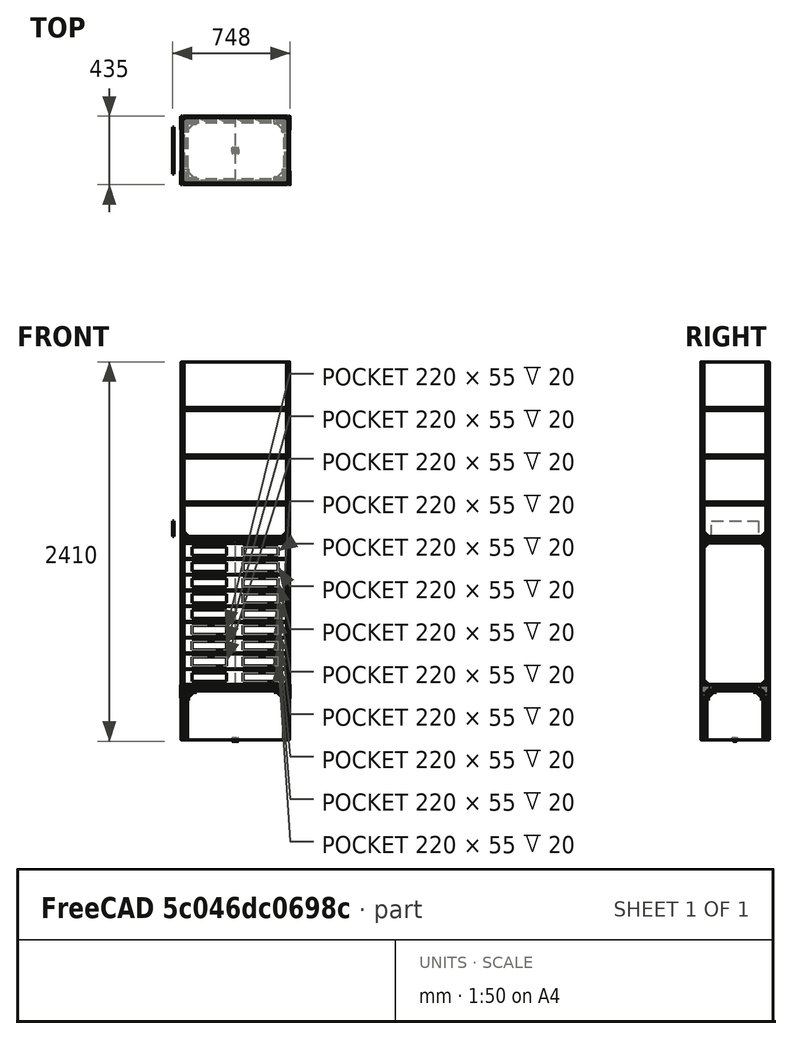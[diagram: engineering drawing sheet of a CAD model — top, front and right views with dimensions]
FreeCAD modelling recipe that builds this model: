
FCSTD DOCUMENT  (FreeCAD 1.0R39109 (Git))
Label: 2020 shelf
License: All rights reserved
objects: Part::FeaturePython×74, PartDesign::SubShapeBinder×16, Sketcher::SketchObject×15, PartDesign::Pad×11, PartDesign::Body×9, App::DocumentObjectGroup×9, PartDesign::Mirrored×7, TechDraw::DrawViewBalloon×7, App::Link×4, TechDraw::DrawProjGroupItem×3, TechDraw::DrawSVGTemplate×2, TechDraw::DrawPage×2, PartDesign::Plane×1, PartDesign::MultiTransform×1, PartDesign::Pocket×1, PartDesign::LinearPattern×1, App::VarSet×1, TechDraw::DrawProjGroup×1
note: 184 computed .brp shape members not serialized (recipe doc carries the construction recipe); baked Part::Feature solids carry a one-line shape summary decoded from their .brp
EXTERNAL_REF file=2020 Parts.FCStd obj=Body
EXTERNAL_REF file=2020 Parts.FCStd obj=Body001
EXTERNAL_REF file=2020 Parts.FCStd obj=Body002
EXTERNAL_REF file=2020 Parts.FCStd obj=Body003

FEATURE [Sketcher::SketchObject] Sketch  label="cabinet projection"
  ArcFitTolerance = 1e-06
  AttachmentSupport = -> [XY_Plane]
  FullyConstrained = true
  MakeInternals = false
  MapMode = 5
  sketch-geometry (5):
    g0: LineSegment StartX=-325 StartY=217.5 StartZ=0 EndX=-325 EndY=-217.5 EndZ=0
    g1: LineSegment StartX=-325 StartY=-217.5 StartZ=0 EndX=325 EndY=-217.5 EndZ=0
    g2: LineSegment StartX=325 StartY=-217.5 StartZ=0 EndX=325 EndY=217.5 EndZ=0
    g3: LineSegment StartX=325 StartY=217.5 StartZ=0 EndX=-325 EndY=217.5 EndZ=0
    g4: GeomPoint [constr] X=0 Y=0 Z=0
  constraints (12):
    c: Coincident(g0,g1)
    c: Coincident(g1,g2)
    c: Coincident(g2,g3)
    c: Coincident(g3,g0)
    c: Vertical(g0)
    c: Vertical(g2)
    c: Horizontal(g1)
    c: Horizontal(g3)
    c: Symmetric(g2,g0,g4)
    c: Coincident(g4,g-1)
    c: DistanceX(g1,g1) = 650
    c: DistanceY(g2,g2) = 435
FEATURE [Sketcher::SketchObject] Sketch001
  ArcFitTolerance = 1e-06
  AttachmentSupport = -> [XY_Plane]
  ExternalGeometry = -> [Sketch]
  FullyConstrained = true
  MakeInternals = false
  MapMode = 5
  sketch-geometry (5):
    g0: LineSegment StartX=335 StartY=207.5 StartZ=0 EndX=-335 EndY=207.5 EndZ=0
    g1: LineSegment StartX=-335 StartY=207.5 StartZ=0 EndX=-335 EndY=-207.5 EndZ=0
    g2: LineSegment StartX=-335 StartY=-207.5 StartZ=0 EndX=335 EndY=-207.5 EndZ=0
    g3: LineSegment StartX=335 StartY=-207.5 StartZ=0 EndX=335 EndY=207.5 EndZ=0
    g4: GeomPoint [constr] X=0 Y=0 Z=0
  constraints (12):
    c: Coincident(g0,g1)
    c: Coincident(g1,g2)
    c: Coincident(g2,g3)
    c: Coincident(g3,g0)
    c: Horizontal(g0)
    c: Horizontal(g2)
    c: Vertical(g1)
    c: Vertical(g3)
    c: Symmetric(g2,g0,g4)
    c: Coincident(g4,g-1)
    c: DistanceY(g-6,g1) = 10
    c: DistanceX(g1,g-6) = 10
FEATURE [PartDesign::Pad] Pad
  Direction = (0,0,1)
  Length = 2400
  Length2 = 10
  Profile = -> Sketch001
  ReferenceAxis = -> Sketch001 [N_Axis]
  Suppressed = false
  Type = 0
FEATURE [PartDesign::SubShapeBinder] Binder
  BindCopyOnChange = 0
  BindMode = 0
  ClaimChildren = false
  Context = -> Body [Binder.]
  Fuse = false
  MakeFace = true
  OffsetFill = false
  OffsetIntersection = false
  OffsetJoinType = 0
  OffsetOpenResult = false
  PartialLoad = false
  Relative = true
  Support = -> [Pad[Edge2,Edge5,Edge8,Edge1]]
  _Version = 2
FEATURE [Sketcher::SketchObject] Sketch002
  ArcFitTolerance = 1e-06
  AttachmentSupport = -> [XY_Plane001]
  FullyConstrained = true
  MakeInternals = false
  MapMode = 5
  sketch-geometry (14):
    g0: LineSegment StartX=0 StartY=3.9 StartZ=0 EndX=2.83934 EndY=3.9 EndZ=0
    g1: LineSegment StartX=2.83934 StartY=3.9 StartZ=0 EndX=5.5 EndY=6.56066 EndZ=0
    g2: LineSegment StartX=5.5 StartY=6.56066 StartZ=0 EndX=5.5 EndY=8 EndZ=0
    g3: LineSegment StartX=5.5 StartY=8 StartZ=0 EndX=3.1 EndY=8 EndZ=0
    g4: LineSegment StartX=3.1 StartY=8 StartZ=0 EndX=3.1 EndY=9.5 EndZ=0
    g5: LineSegment StartX=3.1 StartY=9.5 StartZ=0 EndX=3.6 EndY=9.5 EndZ=0
    g6: LineSegment StartX=3.6 StartY=9.5 StartZ=0 EndX=3.6 EndY=10 EndZ=0
    g7: LineSegment StartX=3.6 StartY=10 StartZ=0 EndX=8.50001 EndY=10 EndZ=0
    g8: LineSegment StartX=0 StartY=0 StartZ=0 EndX=0 EndY=3.9 EndZ=0
    g9: LineSegment [constr] StartX=10 StartY=8.50001 StartZ=0 EndX=10 EndY=0 EndZ=0
    g10: ArcOfCircle [constr] CenterX=8.50001 CenterY=8.50001 CenterZ=0 NormalX=0 NormalY=0 NormalZ=1 AngleXU=0 Radius=1.49999 StartAngle=0 EndAngle=1.5708
    g11: GeomPoint [constr] X=10 Y=10 Z=0
    g12: LineSegment StartX=0 StartY=0 StartZ=0 EndX=9.56066 EndY=9.56066 EndZ=0
    g13: ArcOfCircle CenterX=8.50001 CenterY=8.5 CenterZ=0 NormalX=0 NormalY=0 NormalZ=1 AngleXU=0 Radius=1.5 StartAngle=0.785402 EndAngle=1.57079
  constraints (41):
    c: PointOnObject(g0,g-2)
    c: Horizontal(g0)
    c: Coincident(g0,g1)
    c: Coincident(g1,g2)
    c: Vertical(g2)
    c: Coincident(g2,g3)
    c: Horizontal(g3)
    c: Coincident(g3,g4)
    c: Vertical(g4)
    c: Coincident(g4,g5)
    c: Coincident(g5,g6)
    c: Coincident(g6,g7)
    c: Horizontal(g7)
    c: Coincident(g8,g0)
    c: Vertical(g6)
    c: Horizontal(g5)
    c: Distance(g8,g8) = 3.9
    c: DistanceX(g-1,g11) = 10
    c: DistanceY(g-1,g11) = 10
    c: Distance(g3,g0) = 4.1
    c: Equal(g5,g6)
    c: Distance(g6,g6) = 0.5
    c: DistanceY(g3,g6) = 2
    c: PointOnObject(g9,g-1)
    c: Vertical(g9)
    c: PointOnObject(g11,g7)
    c: PointOnObject(g11,g9)
    c: Tangent(g7,g10) = 1.5708
    c: Tangent(g9,g10) = 1.5708
    c: Coincident(g12,g8)
    c: PointOnObject(g12,g10)
    c: PointOnObject(g10,g12)
    c: Coincident(g13,g7)
    c: Coincident(g13,g12)
    c: Tangent(g13,g10)
    c: Coincident(g8,g-1)
    c: Parallel(g1,g12)
    c: Distance(g0,g12) = 0.75
    c: DistanceX(g-1,g2) = 5.5
    c: DistanceX(g-1,g3) = 3.1
    c: Radius(g13) = 1.5
FEATURE [PartDesign::Pad] Pad001
  Direction = (0,0,1)
  Length = 1
  Length2 = 10
  Profile = -> Sketch002
  ReferenceAxis = -> Sketch002 [N_Axis]
  Suppressed = false
  Type = 0
FEATURE [PartDesign::Plane] DatumPlane
  AttachmentOffset = pos=(0,0,0) rot=(0.862856,0.357407,0.357407;1.71777rad)
  AttachmentSupport = -> [XY_Plane001]
  Length = 82.6027
  MapMode = 5
  Placement = pos=(0,0,0) rot=(0.862856,0.357407,0.357407;1.71777rad)
  ResizeMode = 0
  Width = 61.8921
FEATURE [PartDesign::Mirrored] Mirrored
  MirrorPlane = -> DatumPlane
  Suppressed = false
  TransformMode = 0
FEATURE [PartDesign::Mirrored] Mirrored001
  MirrorPlane = -> YZ_Plane001
  Suppressed = false
  TransformMode = 0
FEATURE [PartDesign::Mirrored] Mirrored002
  MirrorPlane = -> XZ_Plane001
  Suppressed = false
  TransformMode = 0
FEATURE [PartDesign::MultiTransform] MultiTransform
  BaseFeature = -> Pad001
  Refine = true
  Suppressed = false
  TransformMode = 1
  Transformations = -> [Mirrored,Mirrored001,Mirrored002]
FEATURE [PartDesign::SubShapeBinder] Binder001  label="2020 Profile"
  BindCopyOnChange = 0
  BindMode = 0
  ClaimChildren = false
  Context = -> Body001 [Binder001.]
  Fuse = false
  MakeFace = true
  OffsetFill = false
  OffsetIntersection = false
  OffsetJoinType = 0
  OffsetOpenResult = false
  PartialLoad = false
  Relative = true
  Support = -> [MultiTransform[Face34]]
  _Version = 2
FEATURE [PartDesign::Body] Body001  label="2020"
  AllowCompound = true
  Group = -> [Sketch002,Pad001,DatumPlane,MultiTransform,Mirrored,Mirrored001,Mirrored002,Binder001]
  Origin = -> Origin001
  Tip = -> MultiTransform
FEATURE [Part::FeaturePython] Clone  label="2020 Profile001"  # Draft clone (typed FeaturePython)
  AttacherType = Attacher::AttachEngine3D
  Fuse = false
  Objects = -> [Binder001]
  Scale = (1,1,1)
FEATURE [Part::FeaturePython] Clone001  label="Binder001"  # Draft clone (typed FeaturePython)
  AttacherType = Attacher::AttachEngine3D
  Fuse = false
  Objects = -> [Binder]
  Scale = (1,1,1)
FEATURE [Part::FeaturePython] Frame  # Arch/BIM 107 (typed FeaturePython)
  Align = true
  Base = -> Clone001
  BasePoint = 0
  Edges = 0
  Fuse = false
  HorizontalArea = 0
  IfcData = attributes={"GlobalId": {"name": "GlobalId", "type": "IfcGloballyUniqueId", "is_enum": false, "enum_values": []}, "Description": {"... (+458 chars omitted),+1 more (map truncated)
  IfcType = 107
  MoveBase = false
  MoveWithHost = false
  Offset = (0,0,0)
  PerimeterLength = 0
  PredefinedType = 0
  Profile = -> Clone
  Rotation = 0
  VerticalArea = 0
FEATURE [Sketcher::SketchObject] Sketch016
  ArcFitTolerance = 1e-06
  AttachmentSupport = -> [XY_Plane007]
  FullyConstrained = true
  MakeInternals = false
  MapMode = 5
  sketch-geometry (8):
    g0: LineSegment StartX=20 StartY=0 StartZ=0 EndX=305 EndY=0 EndZ=0
    g1: LineSegment StartX=325 StartY=20 StartZ=0 EndX=325 EndY=435 EndZ=0
    g2: LineSegment StartX=325 StartY=435 StartZ=0 EndX=0 EndY=435 EndZ=0
    g3: LineSegment StartX=0 StartY=435 StartZ=0 EndX=0 EndY=20 EndZ=0
    g4: ArcOfCircle CenterX=20 CenterY=20 CenterZ=0 NormalX=0 NormalY=0 NormalZ=1 AngleXU=0 Radius=20 StartAngle=3.14159 EndAngle=4.71239
    g5: GeomPoint [constr] X=0 Y=0 Z=0
    g6: ArcOfCircle CenterX=305 CenterY=20 CenterZ=0 NormalX=0 NormalY=0 NormalZ=1 AngleXU=0 Radius=20 StartAngle=4.71239 EndAngle=6.28319
    g7: GeomPoint [constr] X=325 Y=0 Z=0
  constraints (19):
    c: Coincident(g1,g2)
    c: Coincident(g2,g3)
    c: Horizontal(g0)
    c: Horizontal(g2)
    c: Vertical(g1)
    c: Vertical(g3)
    c: Coincident(g5,g-1)
    c: DistanceX(g5,g7) = 325
    c: DistanceY(g7,g1) = 435
    c: PointOnObject(g5,g3)
    c: PointOnObject(g5,g0)
    c: Tangent(g3,g4) = -1.5708
    c: Tangent(g0,g4) = -1.5708
    c: PointOnObject(g7,g0)
    c: PointOnObject(g7,g1)
    c: Tangent(g0,g6) = -1.5708
    c: Tangent(g1,g6) = -1.5708
    c: Equal(g4,g6)
    c: Radius(g6) = 20
FEATURE [PartDesign::Pad] Pad009
  Direction = (0,0,1)
  Length = 920
  Length2 = 10
  Profile = -> Sketch016
  ReferenceAxis = -> Sketch016 [N_Axis]
  Suppressed = false
  Type = 0
FEATURE [Sketcher::SketchObject] Sketch017
  ArcFitTolerance = 1e-06
  AttachmentSupport = -> [XZ_Plane007]
  FullyConstrained = true
  MakeInternals = false
  MapMode = 5
  Placement = pos=(0,0,0) rot=(1,0,0;1.5708rad)
  sketch-geometry (9):
    g0: LineSegment StartX=50 StartY=75 StartZ=0 EndX=50 EndY=20 EndZ=0
    g1: LineSegment StartX=50 StartY=20 StartZ=0 EndX=270 EndY=20 EndZ=0
    g2: LineSegment StartX=270 StartY=20 StartZ=0 EndX=270 EndY=75 EndZ=0
    g3: LineSegment StartX=270 StartY=75 StartZ=0 EndX=50 EndY=75 EndZ=0
    g4: GeomPoint [constr] X=160 Y=47.5 Z=0
    g5: LineSegment StartX=0 StartY=100 StartZ=0 EndX=0 EndY=95 EndZ=0
    g6: LineSegment StartX=0 StartY=95 StartZ=0 EndX=320 EndY=95 EndZ=0
    g7: LineSegment StartX=320 StartY=95 StartZ=0 EndX=320 EndY=100 EndZ=0
    g8: LineSegment StartX=320 StartY=100 StartZ=0 EndX=0 EndY=100 EndZ=0
  constraints (26):
    c: Coincident(g0,g1)
    c: Coincident(g1,g2)
    c: Coincident(g2,g3)
    c: Coincident(g3,g0)
    c: Vertical(g0)
    c: Vertical(g2)
    c: Horizontal(g1)
    c: Horizontal(g3)
    c: Symmetric(g2,g0,g4)
    c: Coincident(g5,g6)
    c: Coincident(g6,g7)
    c: Coincident(g7,g8)
    c: Coincident(g8,g5)
    c: Vertical(g5)
    c: Vertical(g7)
    c: Horizontal(g6)
    c: Horizontal(g8)
    c: PointOnObject(g5,g-2)
    c: Distance(g8,g8) = 320
    c: DistanceX(g-1,g4) = 160
    c: DistanceX(g-1,g0) = 50
    c: Distance(g0,g6) = 20
    c: DistanceY(g-1,g0) = 20
    c: DistanceY(g0,g0) = 55
    c: DistanceY(g7,g7) = 5
    c: DistanceY(g-1,g7) = 100
FEATURE [PartDesign::Pocket] Pocket002
  BaseFeature = -> Pad009
  Direction = (0,1,-2e-16)
  Length = 20
  Length2 = 5
  Profile = -> Sketch017
  ReferenceAxis = -> Sketch017 [N_Axis]
  Suppressed = false
  Type = 0
FEATURE [PartDesign::LinearPattern] LinearPattern
  BaseFeature = -> Pocket002
  Direction = -> Z_Axis007
  Length = 800
  Mode = 1
  Occurrences = 9
  Offset = 100
  Originals = -> [Pocket002]
  Suppressed = false
  TransformMode = 0
FEATURE [PartDesign::Body] Body007  label="Cabinet"
  AllowCompound = true
  Group = -> [Sketch016,Pad009,Sketch017,Pocket002,LinearPattern]
  Origin = -> Origin007
  Tip = -> LinearPattern
FEATURE [Part::FeaturePython] Clone002  label="Cabinet001"  # Draft clone (typed FeaturePython)
  AttacherType = Attacher::AttachEngine3D
  AttachmentOffset = pos=(0,0,350) rot=(0,0,1;0rad)
  AttachmentSupport = -> [Sketch]
  Fuse = false
  MapMode = 1
  Objects = -> [Body007]
  Placement = pos=(-325,-217.5,350) rot=(0,0,1;0rad)
  Scale = (1,1,1)
  expr: .AttachmentOffset.Base.z = VarSet.StiltHeight
FEATURE [Part::FeaturePython] Clone003  label="Cabinet002"  # Draft clone (typed FeaturePython)
  AttacherType = Attacher::AttachEngine3D
  AttachmentOffset = pos=(325,0,350) rot=(0,0,1;0rad)
  AttachmentSupport = -> [Sketch]
  Fuse = false
  MapMode = 1
  Objects = -> [Body007]
  Placement = pos=(0,-217.5,350) rot=(0,0,1;0rad)
  Scale = (1,1,1)
  expr: .AttachmentOffset.Base.z = VarSet.StiltHeight
FEATURE [Sketcher::SketchObject] Sketch018
  ArcFitTolerance = 1e-06
  AttachmentOffset = pos=(0,0,330) rot=(0,0,1;0rad)
  AttachmentSupport = -> [XY_Plane]
  ExternalGeometry = -> [Binder]
  FullyConstrained = true
  MakeInternals = false
  MapMode = 5
  Placement = pos=(0,0,330) rot=(0,0,1;0rad)
  expr: .AttachmentOffset.Base.z = VarSet.StiltHeight - 20 mm
  sketch-geometry (6):
    g0: LineSegment StartX=-325 StartY=207.5 StartZ=0 EndX=325 EndY=207.5 EndZ=0
    g1: LineSegment StartX=-325 StartY=-207.5 StartZ=0 EndX=325 EndY=-207.5 EndZ=0
    g2: LineSegment StartX=-325 StartY=197.5 StartZ=0 EndX=-325 EndY=-197.5 EndZ=0
    g3: LineSegment StartX=325 StartY=197.5 StartZ=0 EndX=325 EndY=-197.5 EndZ=0
    g4: LineSegment StartX=-305 StartY=187.5 StartZ=0 EndX=305 EndY=187.5 EndZ=0
    g5: LineSegment StartX=-305 StartY=-187.5 StartZ=0 EndX=305 EndY=-187.5 EndZ=0
  constraints (24):
    c: Horizontal(g0)
    c: Horizontal(g1)
    c: Vertical(g0,g1)
    c: Equal(g0,g1)
    c: DistanceX(g-3,g0) = 10
    c: DistanceX(g0,g-4) = 10
    c: Vertical(g2)
    c: Vertical(g3)
    c: Equal(g2,g3)
    c: Horizontal(g2,g3)
    c: Vertical(g0,g2)
    c: Vertical(g0,g3)
    c: Distance(g0,g2) = 10
    c: Distance(g2,g1) = 10
    c: Horizontal(g1,g-6)
    c: Horizontal(g0,g-3)
    c: Horizontal(g4)
    c: Horizontal(g5)
    c: Vertical(g4,g5)
    c: Equal(g4,g5)
    c: Distance(g4,g0) = 20
    c: DistanceX(g0,g4) = 20
    c: DistanceX(g4,g0) = 20
    c: Distance(g5,g1) = 20
FEATURE [App::DocumentObjectGroup] Group003  label="Cabinets"
  Group = -> [Clone002,Clone003]
FEATURE [PartDesign::SubShapeBinder] Binder002
  BindCopyOnChange = 0
  BindMode = 0
  ClaimChildren = false
  Context = -> Body008 [Binder002.]
  Fuse = false
  MakeFace = true
  OffsetFill = false
  OffsetIntersection = false
  OffsetJoinType = 0
  OffsetOpenResult = false
  PartialLoad = false
  Placement = pos=(10,0,0) rot=(0,0,1;0rad)
  Relative = true
  Support = -> [Body001[Binder001.]]
  _Version = 2
FEATURE [PartDesign::Pad] Pad010
  Direction = (0,0,-1)
  Length = 10
  Length2 = 10
  Placement = pos=(10,0,0) rot=(0,0,1;0rad)
  Profile = -> Binder002
  Suppressed = false
  Type = 0
FEATURE [PartDesign::Mirrored] Mirrored003
  BaseFeature = -> Pad010
  MirrorPlane = -> YZ_Plane008
  Placement = pos=(10,0,0) rot=(0,0,1;0rad)
  Refine = true
  Suppressed = false
  TransformMode = 1
FEATURE [Sketcher::SketchObject] Sketch019
  ArcFitTolerance = 1e-06
  AttachmentSupport = -> [XY_Plane008]
  FullyConstrained = true
  MakeInternals = false
  MapMode = 5
  sketch-geometry (5):
    g0: LineSegment StartX=-1.5 StartY=10 StartZ=0 EndX=1.5 EndY=10 EndZ=0
    g1: LineSegment StartX=1.5 StartY=10 StartZ=0 EndX=1.5 EndY=7 EndZ=0
    g2: LineSegment StartX=1.5 StartY=7 StartZ=0 EndX=-1.5 EndY=7 EndZ=0
    g3: LineSegment StartX=-1.5 StartY=7 StartZ=0 EndX=-1.5 EndY=10 EndZ=0
    g4: GeomPoint [constr] X=0 Y=8.5 Z=0
  constraints (13):
    c: Coincident(g0,g1)
    c: Coincident(g1,g2)
    c: Coincident(g2,g3)
    c: Coincident(g3,g0)
    c: Horizontal(g0)
    c: Horizontal(g2)
    c: Vertical(g1)
    c: Vertical(g3)
    c: Symmetric(g2,g0,g4)
    c: PointOnObject(g4,g-2)
    c: Equal(g1,g2)
    c: DistanceX(g2,g2) = 3
    c: DistanceY(g-1,g0) = 10
FEATURE [PartDesign::Pad] Pad011
  BaseFeature = -> Mirrored003
  Direction = (0,0,1)
  Length = 10
  Length2 = 10
  Placement = pos=(10,0,0) rot=(0,0,1;0rad)
  Profile = -> Sketch019
  ReferenceAxis = -> Sketch019 [N_Axis]
  Refine = true
  Reversed = true
  Suppressed = false
  Type = 0
FEATURE [PartDesign::Mirrored] Mirrored004
  BaseFeature = -> Pad011
  MirrorPlane = -> XZ_Plane008
  Originals = -> [Pad011]
  Placement = pos=(10,0,0) rot=(0,0,1;0rad)
  Refine = true
  Suppressed = false
  TransformMode = 0
FEATURE [PartDesign::SubShapeBinder] Binder003  label="2040 Profile"
  BindCopyOnChange = 0
  BindMode = 0
  ClaimChildren = false
  Context = -> Body008 [Binder003.]
  Fuse = false
  MakeFace = true
  OffsetFill = false
  OffsetIntersection = false
  OffsetJoinType = 0
  OffsetOpenResult = false
  PartialLoad = false
  Relative = true
  Support = -> [Mirrored004[Face96]]
  _Version = 2
FEATURE [PartDesign::Body] Body008  label="2040"
  AllowCompound = true
  Group = -> [Binder002,Pad010,Mirrored003,Sketch019,Pad011,Mirrored004,Binder003]
  Origin = -> Origin008
  Tip = -> Mirrored004
FEATURE [PartDesign::SubShapeBinder] Binder004
  BindCopyOnChange = 0
  BindMode = 0
  ClaimChildren = false
  Context = -> Body009 [Binder004.]
  Fuse = false
  MakeFace = true
  OffsetFill = false
  OffsetIntersection = false
  OffsetJoinType = 0
  OffsetOpenResult = false
  PartialLoad = false
  Placement = pos=(0,10,0) rot=(0,0,1;0rad)
  Relative = true
  Support = -> [Body008[Binder003.]]
  _Version = 2
FEATURE [PartDesign::Pad] Pad012
  Direction = (0,0,1)
  Length = 10
  Length2 = 10
  Placement = pos=(0,10,0) rot=(0,0,1;0rad)
  Profile = -> Binder004
  Suppressed = false
  Type = 0
FEATURE [PartDesign::Mirrored] Mirrored005
  BaseFeature = -> Pad012
  MirrorPlane = -> XZ_Plane009
  Placement = pos=(0,10,0) rot=(0,0,1;0rad)
  Refine = true
  Suppressed = false
  TransformMode = 1
FEATURE [Sketcher::SketchObject] Sketch020
  ArcFitTolerance = 1e-06
  AttachmentSupport = -> [XY_Plane009]
  FullyConstrained = true
  MakeInternals = false
  MapMode = 5
  sketch-geometry (5):
    g0: LineSegment StartX=-17 StartY=-1.5 StartZ=0 EndX=-17 EndY=1.5 EndZ=0
    g1: LineSegment StartX=-17 StartY=1.5 StartZ=0 EndX=-20 EndY=1.5 EndZ=0
    g2: LineSegment StartX=-20 StartY=1.5 StartZ=0 EndX=-20 EndY=-1.5 EndZ=0
    g3: LineSegment StartX=-20 StartY=-1.5 StartZ=0 EndX=-17 EndY=-1.5 EndZ=0
    g4: GeomPoint [constr] X=-18.5 Y=0 Z=0
  constraints (13):
    c: Coincident(g0,g1)
    c: Coincident(g1,g2)
    c: Coincident(g2,g3)
    c: Coincident(g3,g0)
    c: Vertical(g0)
    c: Vertical(g2)
    c: Horizontal(g1)
    c: Horizontal(g3)
    c: Symmetric(g2,g0,g4)
    c: PointOnObject(g4,g-1)
    c: Equal(g2,g1)
    c: Distance(g2,g2) = 3
    c: DistanceX(g1,g-1) = 20
FEATURE [PartDesign::Pad] Pad013
  BaseFeature = -> Mirrored005
  Direction = (0,0,1)
  Length = 10
  Length2 = 10
  Placement = pos=(0,10,0) rot=(0,0,1;0rad)
  Profile = -> Sketch020
  ReferenceAxis = -> Sketch020 [N_Axis]
  Refine = true
  Suppressed = false
  Type = 0
FEATURE [PartDesign::Mirrored] Mirrored006
  BaseFeature = -> Pad013
  MirrorPlane = -> Sketch020 [V_Axis]
  Originals = -> [Pad013]
  Placement = pos=(0,10,0) rot=(0,0,1;0rad)
  Refine = true
  Suppressed = false
  TransformMode = 0
FEATURE [PartDesign::SubShapeBinder] Binder005  label="4420 Profile"
  BindCopyOnChange = 0
  BindMode = 0
  ClaimChildren = false
  Context = -> Body009 [Binder005.]
  Fuse = false
  MakeFace = true
  OffsetFill = false
  OffsetIntersection = false
  OffsetJoinType = 0
  OffsetOpenResult = false
  PartialLoad = false
  Relative = true
  Support = -> [Mirrored006[Face124]]
  _Version = 2
FEATURE [PartDesign::Body] Body009  label="4420"
  AllowCompound = true
  Group = -> [Binder004,Pad012,Mirrored005,Sketch020,Pad013,Mirrored006,Binder005]
  Origin = -> Origin009
  Tip = -> Mirrored006
FEATURE [PartDesign::SubShapeBinder] Binder006
  BindCopyOnChange = 0
  BindMode = 0
  ClaimChildren = false
  Context = -> Body010 [Binder006.]
  Fuse = false
  MakeFace = true
  OffsetFill = false
  OffsetIntersection = false
  OffsetJoinType = 0
  OffsetOpenResult = false
  PartialLoad = false
  Relative = true
  Support = -> [Body[Binder.]]
  _Version = 2
FEATURE [Sketcher::SketchObject] Sketch022
  ArcFitTolerance = 1e-06
  AttachmentSupport = -> [XY_Plane010]
  ExternalGeometry = -> [Binder006]
  FullyConstrained = true
  MakeInternals = false
  MapMode = 5
  sketch-geometry (5):
    g0: LineSegment StartX=-335 StartY=-187.5 StartZ=0 EndX=335 EndY=-187.5 EndZ=0
    g1: LineSegment StartX=335 StartY=-187.5 StartZ=0 EndX=335 EndY=187.5 EndZ=0
    g2: LineSegment StartX=335 StartY=187.5 StartZ=0 EndX=-335 EndY=187.5 EndZ=0
    g3: LineSegment StartX=-335 StartY=187.5 StartZ=0 EndX=-335 EndY=-187.5 EndZ=0
    g4: GeomPoint [constr] X=0 Y=0 Z=0
  constraints (12):
    c: Coincident(g0,g1)
    c: Coincident(g1,g2)
    c: Coincident(g2,g3)
    c: Coincident(g3,g0)
    c: Horizontal(g0)
    c: Horizontal(g2)
    c: Vertical(g1)
    c: Vertical(g3)
    c: Symmetric(g2,g0,g4)
    c: Coincident(g4,g-1)
    c: Vertical(g-3,g1)
    c: Distance(g-3,g1) = 20
FEATURE [PartDesign::Pad] Pad014
  Direction = (0,0,1)
  Length = 310
  Length2 = 10
  Profile = -> Sketch022
  ReferenceAxis = -> Sketch022 [N_Axis]
  Suppressed = false
  Type = 0
  expr: Length = VarSet.StiltHeight - 40 mm
FEATURE [PartDesign::SubShapeBinder] Binder007
  BindCopyOnChange = 0
  BindMode = 0
  ClaimChildren = false
  Context = -> Body010 [Binder007.]
  Fuse = false
  MakeFace = true
  OffsetFill = false
  OffsetIntersection = false
  OffsetJoinType = 0
  OffsetOpenResult = false
  PartialLoad = false
  Relative = true
  Support = -> [Pad014[Edge8,Edge1,Edge2,Edge5]]
  _Version = 2
FEATURE [PartDesign::Body] Body010
  AllowCompound = true
  Group = -> [Binder006,Sketch022,Pad014,Binder007]
  Origin = -> Origin010
  Tip = -> Pad014
FEATURE [Part::FeaturePython] Clone006  label="Binder008"  # Draft clone (typed FeaturePython)
  AttacherType = Attacher::AttachEngine3D
  Fuse = false
  Objects = -> [Binder007]
  Scale = (1,1,1)
FEATURE [Part::FeaturePython] Clone007  label="2020 Profile002"  # Draft clone (typed FeaturePython)
  AttacherType = Attacher::AttachEngine3D
  Fuse = false
  Objects = -> [Binder001]
  Scale = (1,1,1)
FEATURE [Part::FeaturePython] Frame003  # Arch/BIM 107 (typed FeaturePython)
  Align = true
  Base = -> Clone006
  BasePoint = 0
  Edges = 0
  Fuse = false
  HorizontalArea = 0
  IfcData = attributes={"GlobalId": {"name": "GlobalId", "type": "IfcGloballyUniqueId", "is_enum": false, "enum_values": []}, "Description": {"... (+458 chars omitted),+1 more (map truncated)
  IfcType = 107
  MoveBase = false
  MoveWithHost = false
  Offset = (0,0,0)
  PerimeterLength = 0
  PredefinedType = 0
  Profile = -> Clone007
  Rotation = 0
  VerticalArea = 0
FEATURE [Sketcher::SketchObject] Sketch023
  ArcFitTolerance = 1e-06
  AttachmentSupport = -> [XY_Plane011]
  FullyConstrained = true
  MakeInternals = false
  MapMode = 5
  sketch-geometry (38):
    g0: LineSegment StartX=-9 StartY=75 StartZ=0 EndX=-9 EndY=-8 EndZ=0
    g1: LineSegment StartX=-8 StartY=-9 StartZ=0 EndX=75 EndY=-9 EndZ=0
    g2: LineSegment StartX=76 StartY=-8 StartZ=0 EndX=76 EndY=28 EndZ=0
    g3: LineSegment StartX=75 StartY=29 StartZ=0 EndX=29 EndY=29 EndZ=0
    g4: LineSegment StartX=29 StartY=29 StartZ=0 EndX=29 EndY=75 EndZ=0
    g5: LineSegment StartX=28 StartY=76 StartZ=0 EndX=-8 EndY=76 EndZ=0
    g6: ArcOfCircle CenterX=-8 CenterY=75 CenterZ=0 NormalX=0 NormalY=0 NormalZ=1 AngleXU=0 Radius=1 StartAngle=1.5708 EndAngle=3.14159
    g7: GeomPoint [constr] X=-9 Y=76 Z=0
    g8: ArcOfCircle CenterX=28 CenterY=75 CenterZ=0 NormalX=0 NormalY=0 NormalZ=1 AngleXU=0 Radius=1 StartAngle=1.8e-15 EndAngle=1.5708
    g9: GeomPoint [constr] X=29 Y=76 Z=0
    g10: ArcOfCircle CenterX=75 CenterY=28 CenterZ=0 NormalX=0 NormalY=0 NormalZ=1 AngleXU=0 Radius=1 StartAngle=1.941e-13 EndAngle=1.5708
    g11: GeomPoint [constr] X=76 Y=29 Z=0
    g12: ArcOfCircle CenterX=75 CenterY=-8 CenterZ=0 NormalX=0 NormalY=0 NormalZ=1 AngleXU=0 Radius=1 StartAngle=4.71239 EndAngle=6.28319
    g13: GeomPoint [constr] X=76 Y=-9 Z=0
    g14: ArcOfCircle CenterX=-8 CenterY=-8 CenterZ=0 NormalX=0 NormalY=0 NormalZ=1 AngleXU=0 Radius=1 StartAngle=3.14159 EndAngle=4.71239
    g15: GeomPoint [constr] X=-9 Y=-9 Z=0
    g16: LineSegment [constr] StartX=0 StartY=66 StartZ=0 EndX=0 EndY=46 EndZ=0
    g17: LineSegment [constr] StartX=0 StartY=46 StartZ=0 EndX=20 EndY=46 EndZ=0
    g18: LineSegment [constr] StartX=20 StartY=46 StartZ=0 EndX=20 EndY=66 EndZ=0
    g19: LineSegment [constr] StartX=20 StartY=66 StartZ=0 EndX=0 EndY=66 EndZ=0
    g20: GeomPoint [constr] X=10 Y=56 Z=0
    g21: LineSegment [constr] StartX=46 StartY=20 StartZ=0 EndX=46 EndY=0 EndZ=0
    g22: LineSegment [constr] StartX=46 StartY=0 StartZ=0 EndX=66 EndY=0 EndZ=0
    g23: LineSegment [constr] StartX=66 StartY=0 StartZ=0 EndX=66 EndY=20 EndZ=0
    g24: LineSegment [constr] StartX=66 StartY=20 StartZ=0 EndX=46 EndY=20 EndZ=0
    g25: GeomPoint [constr] X=56 Y=10 Z=0
    g26: GeomPoint [constr] X=10 Y=76 Z=0
    g27: GeomPoint [constr] X=76 Y=10 Z=0
    g28: LineSegment [constr] StartX=10 StartY=76 StartZ=0 EndX=10 EndY=10 EndZ=0
    g29: LineSegment [constr] StartX=10 StartY=10 StartZ=0 EndX=76 EndY=10 EndZ=0
    g30: Circle CenterX=0 CenterY=66 CenterZ=0 NormalX=0 NormalY=0 NormalZ=1 AngleXU=0 Radius=2.75
    g31: Circle CenterX=20 CenterY=66 CenterZ=0 NormalX=0 NormalY=0 NormalZ=1 AngleXU=0 Radius=2.75
    g32: Circle CenterX=0 CenterY=46 CenterZ=0 NormalX=0 NormalY=0 NormalZ=1 AngleXU=0 Radius=2.75
    g33: Circle CenterX=20 CenterY=46 CenterZ=0 NormalX=0 NormalY=0 NormalZ=1 AngleXU=0 Radius=2.75
    g34: Circle CenterX=46 CenterY=20 CenterZ=0 NormalX=0 NormalY=0 NormalZ=1 AngleXU=0 Radius=2.75
    g35: Circle CenterX=66 CenterY=20 CenterZ=0 NormalX=0 NormalY=0 NormalZ=1 AngleXU=0 Radius=2.75
    g36: Circle CenterX=46 CenterY=0 CenterZ=0 NormalX=0 NormalY=0 NormalZ=1 AngleXU=0 Radius=2.75
    g37: Circle CenterX=66 CenterY=0 CenterZ=0 NormalX=0 NormalY=0 NormalZ=1 AngleXU=0 Radius=2.75
  constraints (87):
    c: Vertical(g0)
    c: Horizontal(g1)
    c: Vertical(g2)
    c: Coincident(g3,g4)
    c: Vertical(g4)
    c: Horizontal(g5)
    c: Horizontal(g3)
    c: DistanceX(g15,g13) = 85
    c: DistanceY(g13,g11) = 38
    c: PointOnObject(g7,g5)
    c: PointOnObject(g7,g0)
    c: Tangent(g5,g6) = -1.5708
    c: Tangent(g0,g6) = -1.5708
    c: PointOnObject(g9,g5)
    c: PointOnObject(g9,g4)
    c: Tangent(g5,g8) = -1.5708
    c: Tangent(g4,g8) = -1.5708
    c: PointOnObject(g11,g3)
    c: PointOnObject(g11,g2)
    c: Tangent(g3,g10) = -1.5708
    c: Tangent(g2,g10) = -1.5708
    c: PointOnObject(g13,g2)
    c: PointOnObject(g13,g1)
    c: Tangent(g2,g12) = -1.5708
    c: Tangent(g1,g12) = -1.5708
    c: PointOnObject(g15,g0)
    c: PointOnObject(g15,g1)
    c: Tangent(g0,g14) = -1.5708
    c: Tangent(g1,g14) = -1.5708
    c: Equal(g6,g8)
    c: Equal(g8,g10)
    c: Equal(g10,g12)
    c: Equal(g12,g14)
    c: Radius(g6) = 1
    c: Equal(g0,g1)
    c: Equal(g5,g2)
    c: Coincident(g16,g17)
    c: Coincident(g17,g18)
    c: Coincident(g18,g19)
    c: Coincident(g19,g16)
    c: Vertical(g16)
    c: Vertical(g18)
    c: Horizontal(g17)
    c: Horizontal(g19)
    c: Symmetric(g18,g16,g20)
    c: Coincident(g21,g22)
    c: Coincident(g22,g23)
    c: Coincident(g23,g24)
    c: Coincident(g24,g21)
    c: Vertical(g21)
    c: Vertical(g23)
    c: Horizontal(g22)
    c: Horizontal(g24)
    c: Symmetric(g23,g21,g25)
    c: Symmetric(g5,g5,g26)
    c: Symmetric(g2,g2,g27)
    c: Coincident(g28,g26)
    c: Vertical(g28)
    c: Coincident(g29,g28)
    c: Coincident(g29,g27)
    c: Horizontal(g29)
    c: Equal(g22,g23)
    c: Equal(g17,g18)
    c: Equal(g17,g24)
    c: PointOnObject(g25,g29)
    c: PointOnObject(g20,g28)
    c: Distance(g19,g19) = 20
    c: Distance(g16,g1) = 55
    c: Distance(g21,g0) = 55
    c: Coincident(g30,g16)
    c: Coincident(g31,g18)
    c: Coincident(g32,g16)
    c: Coincident(g33,g17)
    c: Coincident(g34,g21)
    c: Coincident(g35,g23)
    c: Coincident(g36,g21)
    c: Coincident(g37,g22)
    c: Equal(g30,g31)
    c: Equal(g31,g32)
    c: Equal(g32,g33)
    c: Equal(g33,g34)
    c: Equal(g34,g35)
    c: Equal(g35,g36)
    c: Equal(g36,g37)
    c: Diameter(g31) = 5.5
    c: PointOnObject(g16,g-2)
    c: PointOnObject(g21,g-1)
FEATURE [PartDesign::Pad] Pad015
  Direction = (0,0,1)
  Length = 3
  Length2 = 10
  Profile = -> Sketch023
  ReferenceAxis = -> Sketch023 [N_Axis]
  Suppressed = false
  Type = 0
FEATURE [PartDesign::Body] Body011  label="TPDD-2040L-"
  AllowCompound = true
  Group = -> [Sketch023,Pad015]
  Origin = -> Origin011
  Tip = -> Pad015
FEATURE [Part::FeaturePython] Clone008  label="TPDD-2040L-001"  # Draft clone (typed FeaturePython)
  AttacherType = Attacher::AttachEngine3D
  AttachmentOffset = pos=(0,10,20) rot=(0,0,1;3.14159rad)
  AttachmentSupport = -> [Sketch018,Binder]
  Fuse = false
  MapMode = 49
  Objects = -> [Body011]
  Placement = pos=(-345,-207.5,340) rot=(-0.57735,-0.57735,0.57735;2.0944rad)
  Scale = (1,1,1)
FEATURE [Part::FeaturePython] Clone009  label="TPDD-2040L-002"  # Draft clone (typed FeaturePython)
  AttacherType = Attacher::AttachEngine3D
  AttachmentOffset = pos=(0,10,20) rot=(0,0,-1;1.5708rad)
  AttachmentSupport = -> [Sketch018,Binder]
  Fuse = false
  MapMode = 49
  Objects = -> [Body011]
  Placement = pos=(-345,207.5,340) rot=(0.707107,0,-0.707107;3.14159rad)
  Scale = (1,1,1)
FEATURE [Part::FeaturePython] Clone010  label="TPDD-2040L-003"  # Draft clone (typed FeaturePython)
  AttacherType = Attacher::AttachEngine3D
  AttachmentOffset = pos=(10,0,20) rot=(0,0,1;3.14159rad)
  AttachmentSupport = -> [Sketch018,Binder]
  Fuse = false
  MapMode = 52
  Objects = -> [Body011]
  Placement = pos=(345,-207.5,340) rot=(0,-1,0;4.71239rad)
  Scale = (1,1,1)
FEATURE [Part::FeaturePython] Clone011  label="TPDD-2040L-004"  # Draft clone (typed FeaturePython)
  AttacherType = Attacher::AttachEngine3D
  AttachmentOffset = pos=(0,10,20) rot=(0,0,1;3.14159rad)
  AttachmentSupport = -> [Sketch018,Binder]
  Fuse = false
  MapMode = 49
  Objects = -> [Body011]
  Placement = pos=(345,207.5,340) rot=(0.57735,-0.57735,0.57735;4.18879rad)
  Scale = (1,1,1)
FEATURE [App::DocumentObjectGroup] Group004  label="TPDD-2040L"
  Group = -> [Clone008,Clone009,Clone010,Clone011]
FEATURE [App::Link] Link  label="TPDC-6034-"
  LinkedObject = -> <external 2020 Parts.FCStd>#Body
FEATURE [App::VarSet] VarSet
  StiltHeight = 350
FEATURE [PartDesign::SubShapeBinder] Binder008  label="Binder009"
  BindCopyOnChange = 0
  BindMode = 0
  ClaimChildren = false
  Context = -> Body [Binder008.]
  Fuse = false
  MakeFace = true
  OffsetFill = false
  OffsetIntersection = false
  OffsetJoinType = 0
  OffsetOpenResult = false
  PartialLoad = false
  Relative = true
  Support = -> [Sketch018[Edge1,Edge2]]
  _Version = 2
FEATURE [Part::FeaturePython] Clone012  label="TPDC-6034-001"  # Draft clone (typed FeaturePython)
  AttacherType = Attacher::AttachEngine3D
  AttachmentOffset = pos=(20,-10,-10) rot=(1,0,0;3.14159rad)
  AttachmentSupport = -> [Binder008,Binder]
  Fuse = false
  MapMode = 49
  Objects = -> [Link]
  Placement = pos=(-305,-197.5,320) rot=(1,0,0;4.71239rad)
  Scale = (1,1,1)
FEATURE [Part::FeaturePython] Clone013  label="TPDC-6034-002"  # Draft clone (typed FeaturePython)
  AttacherType = Attacher::AttachEngine3D
  AttachmentOffset = pos=(-20,-10,-10) rot=(0,0,1;3.14159rad)
  AttachmentSupport = -> [Binder008,Binder]
  Fuse = false
  MapMode = 49
  Objects = -> [Link]
  Placement = pos=(305,-197.5,320) rot=(0,-0.707107,0.707107;3.14159rad)
  Scale = (1,1,1)
FEATURE [Part::FeaturePython] Clone016  label="Binder010"  # Draft clone (typed FeaturePython)
  AttacherType = Attacher::AttachEngine3D
  Fuse = false
  Objects = -> [Binder008]
  Scale = (1,1,1)
FEATURE [Part::FeaturePython] Clone017  label="2040 Profile001"  # Draft clone (typed FeaturePython)
  AttacherType = Attacher::AttachEngine3D
  Fuse = false
  Objects = -> [Binder003]
  Scale = (1,1,1)
FEATURE [Part::FeaturePython] Frame004  # Arch/BIM 107 (typed FeaturePython)
  Align = true
  Base = -> Clone016
  BasePoint = 0
  Edges = 0
  Fuse = false
  HorizontalArea = 0
  IfcData = attributes={"GlobalId": {"name": "GlobalId", "type": "IfcGloballyUniqueId", "is_enum": false, "enum_values": []}, "Description": {"... (+458 chars omitted),+1 more (map truncated)
  IfcType = 107
  MoveBase = false
  MoveWithHost = false
  Offset = (0,0,0)
  PerimeterLength = 0
  PredefinedType = 0
  Profile = -> Clone017
  Rotation = 90
  VerticalArea = 0
FEATURE [PartDesign::SubShapeBinder] Binder009  label="Binder011"
  BindCopyOnChange = 0
  BindMode = 0
  ClaimChildren = false
  Context = -> Body [Binder009.]
  Fuse = false
  MakeFace = true
  OffsetFill = false
  OffsetIntersection = false
  OffsetJoinType = 0
  OffsetOpenResult = false
  PartialLoad = false
  Relative = true
  Support = -> [Sketch018[Edge3,Edge4]]
  _Version = 2
FEATURE [Part::FeaturePython] Clone018  label="Binder012"  # Draft clone (typed FeaturePython)
  AttacherType = Attacher::AttachEngine3D
  Fuse = false
  Objects = -> [Binder009]
  Scale = (1,1,1)
FEATURE [Part::FeaturePython] Clone019  label="4420 Profile001"  # Draft clone (typed FeaturePython)
  AttacherType = Attacher::AttachEngine3D
  Fuse = false
  Objects = -> [Binder005]
  Scale = (1,1,1)
FEATURE [Part::FeaturePython] Frame005  # Arch/BIM 107 (typed FeaturePython)
  Align = true
  Base = -> Clone018
  BasePoint = 0
  Edges = 0
  Fuse = false
  HorizontalArea = 0
  IfcData = attributes={"GlobalId": {"name": "GlobalId", "type": "IfcGloballyUniqueId", "is_enum": false, "enum_values": []}, "Description": {"... (+458 chars omitted),+1 more (map truncated)
  IfcType = 107
  MoveBase = false
  MoveWithHost = false
  Offset = (0,0,0)
  PerimeterLength = 0
  PredefinedType = 0
  Profile = -> Clone019
  Rotation = 0
  VerticalArea = 0
FEATURE [Sketcher::SketchObject] Sketch024
  ArcFitTolerance = 1e-06
  AttachmentOffset = pos=(0,0,-400) rot=(0,0,1;0rad)
  AttachmentSupport = -> [YZ_Plane012]
  FullyConstrained = true
  MakeInternals = false
  MapMode = 5
  Placement = pos=(-400,0,0) rot=(0.57735,0.57735,0.57735;2.0944rad)
  sketch-geometry (5):
    g0: LineSegment StartX=150 StartY=1290 StartZ=0 EndX=-150 EndY=1290 EndZ=0
    g1: LineSegment StartX=-150 StartY=1290 StartZ=0 EndX=-150 EndY=1390 EndZ=0
    g2: LineSegment StartX=-150 StartY=1390 StartZ=0 EndX=150 EndY=1390 EndZ=0
    g3: LineSegment StartX=150 StartY=1390 StartZ=0 EndX=150 EndY=1290 EndZ=0
    g4: GeomPoint [constr] X=1e-16 Y=1340 Z=0
  constraints (13):
    c: Coincident(g0,g1)
    c: Coincident(g1,g2)
    c: Coincident(g2,g3)
    c: Coincident(g3,g0)
    c: Horizontal(g0)
    c: Horizontal(g2)
    c: Vertical(g1)
    c: Vertical(g3)
    c: Symmetric(g2,g0,g4)
    c: PointOnObject(g4,g-2)
    c: Distance(g1,g1) = 100
    c: Distance(g2,g2) = 300
    c: DistanceY(g-1,g0) = 1290
FEATURE [PartDesign::Pad] Pad016
  Direction = (1,0,0)
  Length = 10
  Length2 = 10
  Placement = pos=(0,0,0) rot=(1,1,1;2.0944rad)
  Profile = -> Sketch024
  ReferenceAxis = -> Sketch024 [N_Axis]
  Suppressed = false
  Type = 0
FEATURE [PartDesign::Body] Body012  label="Panels"
  AllowCompound = true
  Group = -> [Sketch024,Pad016]
  Origin = -> Origin012
  Tip = -> Pad016
FEATURE [PartDesign::SubShapeBinder] Binder010  label="Binder013"
  BindCopyOnChange = 0
  BindMode = 0
  ClaimChildren = false
  Context = -> Body [Binder010.]
  Fuse = false
  MakeFace = true
  OffsetFill = false
  OffsetIntersection = false
  OffsetJoinType = 0
  OffsetOpenResult = false
  PartialLoad = false
  Relative = true
  Support = -> [Sketch018[Edge5,Edge6]]
  _Version = 2
FEATURE [Part::FeaturePython] Clone020  label="Binder014"  # Draft clone (typed FeaturePython)
  AttacherType = Attacher::AttachEngine3D
  Fuse = false
  Objects = -> [Binder010]
  Scale = (1,1,1)
FEATURE [Part::FeaturePython] Clone021  label="2040 Profile002"  # Draft clone (typed FeaturePython)
  AttacherType = Attacher::AttachEngine3D
  Fuse = false
  Objects = -> [Binder003]
  Scale = (1,1,1)
FEATURE [Part::FeaturePython] Frame006  # Arch/BIM 107 (typed FeaturePython)
  Align = true
  Base = -> Clone020
  BasePoint = 0
  Edges = 0
  Fuse = false
  HorizontalArea = 0
  IfcData = attributes={"GlobalId": {"name": "GlobalId", "type": "IfcGloballyUniqueId", "is_enum": false, "enum_values": []}, "Description": {"... (+458 chars omitted),+1 more (map truncated)
  IfcType = 107
  MoveBase = false
  MoveWithHost = false
  Offset = (0,0,0)
  PerimeterLength = 0
  PredefinedType = 0
  Profile = -> Clone021
  Rotation = 90
  VerticalArea = 0
FEATURE [Part::FeaturePython] Clone022  label="TPDC-6034-005"  # Draft clone (typed FeaturePython)
  AttacherType = Attacher::AttachEngine3D
  AttachmentSupport = -> [Sketch018]
  Fuse = false
  MapMode = 49
  Objects = -> [Link]
  Placement = pos=(-305,187.5,330) rot=(1,0,0;3.14159rad)
  Scale = (1,1,1)
FEATURE [Part::FeaturePython] Clone023  label="TPDC-6034-006"  # Draft clone (typed FeaturePython)
  AttacherType = Attacher::AttachEngine3D
  AttachmentOffset = pos=(0,0,0) rot=(1,0,0;3.14159rad)
  AttachmentSupport = -> [Sketch018]
  Fuse = false
  MapMode = 49
  Objects = -> [Link]
  Placement = pos=(-305,-187.5,330) rot=(0,0,1;0rad)
  Scale = (1,1,1)
FEATURE [Part::FeaturePython] Clone024  label="TPDC-6034-007"  # Draft clone (typed FeaturePython)
  AttacherType = Attacher::AttachEngine3D
  AttachmentOffset = pos=(0,0,0) rot=(0,1,0;3.14159rad)
  AttachmentSupport = -> [Sketch018]
  Fuse = false
  MapMode = 49
  Objects = -> [Link]
  Placement = pos=(305,187.5,330) rot=(0,0,1;3.14159rad)
  Scale = (1,1,1)
FEATURE [Part::FeaturePython] Clone025  label="TPDC-6034-008"  # Draft clone (typed FeaturePython)
  AttacherType = Attacher::AttachEngine3D
  AttachmentOffset = pos=(0,0,0) rot=(0,0,1;3.14159rad)
  AttachmentSupport = -> [Sketch018]
  Fuse = false
  MapMode = 49
  Objects = -> [Link]
  Placement = pos=(305,-187.5,330) rot=(0,-1,0;3.14159rad)
  Scale = (1,1,1)
FEATURE [Sketcher::SketchObject] Sketch025
  ArcFitTolerance = 1e-06
  AttachmentOffset = pos=(0,0,1270) rot=(0,0,1;0rad)
  AttachmentSupport = -> [XY_Plane]
  ExternalGeometry = -> [Binder]
  FullyConstrained = true
  MakeInternals = false
  MapMode = 5
  Placement = pos=(0,0,1270) rot=(0,0,1;0rad)
  sketch-geometry (2):
    g0: LineSegment StartX=-335 StartY=197.5 StartZ=0 EndX=-335 EndY=-197.5 EndZ=0
    g1: LineSegment StartX=335 StartY=197.5 StartZ=0 EndX=335 EndY=-197.5 EndZ=0
  constraints (8):
    c: Vertical(g0)
    c: Vertical(g1)
    c: Horizontal(g0,g1)
    c: Equal(g0,g1)
    c: Vertical(g-3,g0)
    c: Vertical(g-4,g1)
    c: Distance(g-3,g0) = 10
    c: Distance(g0,g-5) = 10
FEATURE [Sketcher::SketchObject] Sketch026
  ArcFitTolerance = 1e-06
  AttachmentOffset = pos=(0,0,1280) rot=(0,0,1;0rad)
  AttachmentSupport = -> [XY_Plane]
  ExternalGeometry = -> [Binder]
  FullyConstrained = true
  MakeInternals = false
  MapMode = 5
  Placement = pos=(0,0,1280) rot=(0,0,1;0rad)
  sketch-geometry (2):
    g0: LineSegment StartX=-325 StartY=207.5 StartZ=0 EndX=325 EndY=207.5 EndZ=0
    g1: LineSegment StartX=-325 StartY=-207.5 StartZ=0 EndX=325 EndY=-207.5 EndZ=0
  constraints (8):
    c: Horizontal(g0)
    c: Horizontal(g1)
    c: Horizontal(g0,g-3)
    c: Horizontal(g-5,g1)
    c: Equal(g0,g1)
    c: Vertical(g0,g1)
    c: Distance(g0,g-3) = 10
    c: Distance(g0,g-4) = 10
FEATURE [Part::FeaturePython] Clone026  label="2040 Profile003"  # Draft clone (typed FeaturePython)
  AttacherType = Attacher::AttachEngine3D
  Fuse = false
  Objects = -> [Binder003]
  Scale = (1,1,1)
FEATURE [Part::FeaturePython] Clone027  label="2020 Profile003"  # Draft clone (typed FeaturePython)
  AttacherType = Attacher::AttachEngine3D
  Fuse = false
  Objects = -> [Binder001]
  Scale = (1,1,1)
FEATURE [App::Link] Link003  label="TPDB-2020-"
  LinkedObject = -> <external 2020 Parts.FCStd>#Body001
FEATURE [Part::FeaturePython] Clone028  label="TPDB-2020-001"  # Draft clone (typed FeaturePython)
  AttacherType = Attacher::AttachEngine3D
  AttachmentOffset = pos=(0,10,10) rot=(0,0,1;0rad)
  AttachmentSupport = -> [Sketch018,Binder]
  Fuse = false
  MapMode = 49
  Objects = -> [Link003]
  Placement = pos=(335,-197.5,340) rot=(0.57735,0.57735,0.57735;2.0944rad)
  Scale = (1,1,1)
FEATURE [Part::FeaturePython] Clone029  label="TPDB-2020-002"  # Draft clone (typed FeaturePython)
  AttacherType = Attacher::AttachEngine3D
  AttachmentOffset = pos=(0,10,-10) rot=(0,0,1;0rad)
  AttachmentSupport = -> [Clone018,Clone001]
  Fuse = false
  MapMode = 49
  Objects = -> [Link003]
  Placement = pos=(335,197.5,340) rot=(0.57735,-0.57735,-0.57735;2.0944rad)
  Scale = (1,1,1)
FEATURE [PartDesign::SubShapeBinder] Binder011  label="Binder015"
  BindCopyOnChange = 0
  BindMode = 0
  ClaimChildren = false
  Context = -> Body [Binder011.]
  Fuse = false
  MakeFace = true
  OffsetFill = false
  OffsetIntersection = false
  OffsetJoinType = 0
  OffsetOpenResult = false
  PartialLoad = false
  Relative = true
  Support = -> [Sketch025]
  _Version = 2
FEATURE [PartDesign::SubShapeBinder] Binder012  label="Binder016"
  BindCopyOnChange = 0
  BindMode = 0
  ClaimChildren = false
  Context = -> Body [Binder012.]
  Fuse = false
  MakeFace = true
  OffsetFill = false
  OffsetIntersection = false
  OffsetJoinType = 0
  OffsetOpenResult = false
  PartialLoad = false
  Relative = true
  Support = -> [Sketch026]
  _Version = 2
FEATURE [Part::FeaturePython] Clone030  label="Binder017"  # Draft clone (typed FeaturePython)
  AttacherType = Attacher::AttachEngine3D
  Fuse = false
  Objects = -> [Binder011]
  Scale = (1,1,1)
FEATURE [Part::FeaturePython] Frame009  # Arch/BIM 107 (typed FeaturePython)
  Align = true
  Base = -> Clone030
  BasePoint = 0
  Edges = 0
  Fuse = false
  HorizontalArea = 0
  IfcData = attributes={"GlobalId": {"name": "GlobalId", "type": "IfcGloballyUniqueId", "is_enum": false, "enum_values": []}, "Description": {"... (+458 chars omitted),+1 more (map truncated)
  IfcType = 107
  MoveBase = false
  MoveWithHost = false
  Offset = (0,0,0)
  PerimeterLength = 0
  PredefinedType = 0
  Profile = -> Clone026
  Rotation = 90
  VerticalArea = 0
FEATURE [Part::FeaturePython] Clone031  label="Binder018"  # Draft clone (typed FeaturePython)
  AttacherType = Attacher::AttachEngine3D
  Fuse = false
  Objects = -> [Binder012]
  Scale = (1,1,1)
FEATURE [Part::FeaturePython] Frame010  # Arch/BIM 107 (typed FeaturePython)
  Align = true
  Base = -> Clone031
  BasePoint = 0
  Edges = 0
  Fuse = false
  HorizontalArea = 0
  IfcData = attributes={"GlobalId": {"name": "GlobalId", "type": "IfcGloballyUniqueId", "is_enum": false, "enum_values": []}, "Description": {"... (+458 chars omitted),+1 more (map truncated)
  IfcType = 107
  MoveBase = false
  MoveWithHost = false
  Offset = (0,0,0)
  PerimeterLength = 0
  PredefinedType = 0
  Profile = -> Clone027
  Rotation = 0
  VerticalArea = 0
FEATURE [Part::FeaturePython] Clone032  label="TPDB-2020-003"  # Draft clone (typed FeaturePython)
  AttacherType = Attacher::AttachEngine3D
  AttachmentOffset = pos=(0,-10,0) rot=(0,0,1;3.14159rad)
  AttachmentSupport = -> [Clone030,Clone001]
  Fuse = false
  MapMode = 49
  Objects = -> [Link003]
  Placement = pos=(335,-197.5,1260) rot=(-0.57735,-0.57735,0.57735;2.0944rad)
  Scale = (1,1,1)
FEATURE [Part::FeaturePython] Clone033  label="TPDB-2020-004"  # Draft clone (typed FeaturePython)
  AttacherType = Attacher::AttachEngine3D
  AttachmentOffset = pos=(0,-10,0) rot=(1,0,0;3.14159rad)
  AttachmentSupport = -> [Clone030,Clone001]
  Fuse = false
  MapMode = 49
  Objects = -> [Link003]
  Placement = pos=(335,197.5,1260) rot=(0.57735,-0.57735,0.57735;4.18879rad)
  Scale = (1,1,1)
FEATURE [Part::FeaturePython] Clone034  label="TPDB-2020-005"  # Draft clone (typed FeaturePython)
  AttacherType = Attacher::AttachEngine3D
  AttachmentOffset = pos=(0,-10,0) rot=(1,0,0;3.14159rad)
  AttachmentSupport = -> [Clone030,Clone001]
  Fuse = false
  MapMode = 49
  Objects = -> [Link003]
  Placement = pos=(-335,197.5,1260) rot=(0.57735,-0.57735,0.57735;4.18879rad)
  Scale = (1,1,1)
FEATURE [Part::FeaturePython] Clone035  label="TPDB-2020-006"  # Draft clone (typed FeaturePython)
  AttacherType = Attacher::AttachEngine3D
  AttachmentOffset = pos=(0,-10,0) rot=(0,0,1;3.14159rad)
  AttachmentSupport = -> [Clone030,Clone001]
  Fuse = false
  MapMode = 49
  Objects = -> [Link003]
  Placement = pos=(-335,-197.5,1260) rot=(-0.57735,-0.57735,0.57735;2.0944rad)
  Scale = (1,1,1)
FEATURE [Part::FeaturePython] Clone036  label="TPDB-2020-007"  # Draft clone (typed FeaturePython)
  AttacherType = Attacher::AttachEngine3D
  AttachmentOffset = pos=(0,10,10) rot=(0,0,1;0rad)
  AttachmentSupport = -> [Clone018,Clone001]
  Fuse = false
  MapMode = 49
  Objects = -> [Link003]
  Placement = pos=(-335,197.5,340) rot=(0.57735,-0.57735,-0.57735;2.0944rad)
  Scale = (1,1,1)
FEATURE [Part::FeaturePython] Clone037  label="TPDB-2020-008"  # Draft clone (typed FeaturePython)
  AttacherType = Attacher::AttachEngine3D
  AttachmentOffset = pos=(0,10,-10) rot=(0,0,1;0rad)
  AttachmentSupport = -> [Clone018,Clone001]
  Fuse = false
  MapMode = 49
  Objects = -> [Link003]
  Placement = pos=(-335,-197.5,340) rot=(0.57735,0.57735,0.57735;2.0944rad)
  Scale = (1,1,1)
FEATURE [Part::FeaturePython] Clone038  label="TPDB-2020-009"  # Draft clone (typed FeaturePython)
  AttacherType = Attacher::AttachEngine3D
  AttachmentSupport = -> [Clone031,Clone030]
  Fuse = false
  MapMode = 49
  Objects = -> [Link003]
  Placement = pos=(-325,207.5,1280) rot=(1,0,0;3.14159rad)
  Scale = (1,1,1)
FEATURE [Part::FeaturePython] Clone039  label="TPDB-2020-010"  # Draft clone (typed FeaturePython)
  AttacherType = Attacher::AttachEngine3D
  AttachmentOffset = pos=(0,0,0) rot=(0,0,1;3.14159rad)
  AttachmentSupport = -> [Clone031,Clone030]
  Fuse = false
  MapMode = 49
  Objects = -> [Link003]
  Placement = pos=(-325,-207.5,1280) rot=(0,0,1;0rad)
  Scale = (1,1,1)
FEATURE [Part::FeaturePython] Clone040  label="TPDB-2020-011"  # Draft clone (typed FeaturePython)
  AttacherType = Attacher::AttachEngine3D
  AttachmentSupport = -> [Clone031,Clone030]
  Fuse = false
  MapMode = 49
  Objects = -> [Link003]
  Placement = pos=(325,207.5,1280) rot=(0,0,1;3.14159rad)
  Scale = (1,1,1)
FEATURE [Part::FeaturePython] Clone041  label="TPDB-2020-012"  # Draft clone (typed FeaturePython)
  AttacherType = Attacher::AttachEngine3D
  AttachmentOffset = pos=(0,0,0) rot=(0,0,1;3.14159rad)
  AttachmentSupport = -> [Clone031,Clone030]
  Fuse = false
  MapMode = 49
  Objects = -> [Link003]
  Placement = pos=(325,-207.5,1280) rot=(0,-1,0;3.14159rad)
  Scale = (1,1,1)
FEATURE [App::Link] Link004  label="TPDD-2020T-"
  LinkedObject = -> <external 2020 Parts.FCStd>#Body002
FEATURE [App::DocumentObjectGroup] Group007  label="TPDD-2020T"
FEATURE [App::Link] Link005  label="TPDG-D5-"
  LinkedObject = -> <external 2020 Parts.FCStd>#Body003
FEATURE [App::DocumentObjectGroup] Group001  label="Parts"
  Group = -> [Body001,Body007,Body008,Body009,Body011,Link,Link003,Link004,Link005]
FEATURE [Part::FeaturePython] Clone042  label="TPDG-D5-001"  # Draft clone (typed FeaturePython)
  AttacherType = Attacher::AttachEngine3D
  AttachmentOffset = pos=(0,10,0) rot=(0,0,1;0rad)
  AttachmentSupport = -> [Clone016,Clone001]
  Fuse = false
  MapMode = 49
  Objects = -> [Link005]
  Placement = pos=(-325,-207.5,340) rot=(1,0,0;1.5708rad)
  Scale = (1,1,1)
FEATURE [Part::FeaturePython] Clone043  label="TPDG-D5-002"  # Draft clone (typed FeaturePython)
  AttacherType = Attacher::AttachEngine3D
  AttachmentOffset = pos=(0,10,0) rot=(0,0,1;0rad)
  AttachmentSupport = -> [Clone016,Clone001]
  Fuse = false
  MapMode = 49
  Objects = -> [Link005]
  Placement = pos=(325,-207.5,340) rot=(0,0.707107,0.707107;3.14159rad)
  Scale = (1,1,1)
FEATURE [Part::FeaturePython] Clone044  label="TPDG-D5-003"  # Draft clone (typed FeaturePython)
  AttacherType = Attacher::AttachEngine3D
  AttachmentOffset = pos=(0,0,0) rot=(1,0,0;3.14159rad)
  AttachmentSupport = -> [Clone031,Clone001]
  Fuse = false
  MapMode = 49
  Objects = -> [Link005]
  Placement = pos=(-325,-207.5,1280) rot=(1,0,0;4.71239rad)
  Scale = (1,1,1)
FEATURE [Part::FeaturePython] Clone045  label="TPDG-D5-004"  # Draft clone (typed FeaturePython)
  AttacherType = Attacher::AttachEngine3D
  AttachmentOffset = pos=(0,0,0) rot=(1,0,0;3.14159rad)
  AttachmentSupport = -> [Clone031,Clone001]
  Fuse = false
  MapMode = 49
  Objects = -> [Link005]
  Placement = pos=(325,-207.5,1280) rot=(0,0.707107,-0.707107;3.14159rad)
  Scale = (1,1,1)
FEATURE [Part::FeaturePython] Clone046  label="TPDG-D5-005"  # Draft clone (typed FeaturePython)
  AttacherType = Attacher::AttachEngine3D
  AttachmentOffset = pos=(0,10,0) rot=(0,0,1;0rad)
  AttachmentSupport = -> [Clone016,Clone001]
  Fuse = false
  MapMode = 49
  Objects = -> [Link005]
  Placement = pos=(325,207.5,340) rot=(0,0.707107,0.707107;3.14159rad)
  Scale = (1,1,1)
FEATURE [Part::FeaturePython] Clone047  label="TPDG-D5-006"  # Draft clone (typed FeaturePython)
  AttacherType = Attacher::AttachEngine3D
  AttachmentOffset = pos=(0,10,0) rot=(0,0,1;0rad)
  AttachmentSupport = -> [Clone016,Clone001]
  Fuse = false
  MapMode = 49
  Objects = -> [Link005]
  Placement = pos=(-325,207.5,340) rot=(1,0,0;1.5708rad)
  Scale = (1,1,1)
FEATURE [Part::FeaturePython] Clone048  label="TPDG-D5-007"  # Draft clone (typed FeaturePython)
  AttacherType = Attacher::AttachEngine3D
  AttachmentOffset = pos=(0,0,0) rot=(1,0,0;3.14159rad)
  AttachmentSupport = -> [Clone031,Clone001]
  Fuse = false
  MapMode = 49
  Objects = -> [Link005]
  Placement = pos=(325,207.5,1280) rot=(0,0.707107,-0.707107;3.14159rad)
  Scale = (1,1,1)
FEATURE [Part::FeaturePython] Clone049  label="TPDG-D5-008"  # Draft clone (typed FeaturePython)
  AttacherType = Attacher::AttachEngine3D
  AttachmentOffset = pos=(0,0,0) rot=(1,0,0;3.14159rad)
  AttachmentSupport = -> [Clone031,Clone001]
  Fuse = false
  MapMode = 49
  Objects = -> [Link005]
  Placement = pos=(-325,207.5,1280) rot=(1,0,0;4.71239rad)
  Scale = (1,1,1)
FEATURE [App::DocumentObjectGroup] Group008  label="TPDG-D5"
  Group = -> [Clone042,Clone043,Clone044,Clone045,Clone046,Clone047,Clone048,Clone049]
FEATURE [Part::FeaturePython] Clone050  label="TPDB-2020-013"  # Draft clone (typed FeaturePython)
  AttacherType = Attacher::AttachEngine3D
  AttachmentSupport = -> [Clone031,Clone001]
  Fuse = false
  MapMode = 49
  Objects = -> [Link003]
  Placement = pos=(-325,-207.5,1280) rot=(1,0,0;1.5708rad)
  Scale = (1,1,1)
FEATURE [Part::FeaturePython] Clone051  label="TPDB-2020-014"  # Draft clone (typed FeaturePython)
  AttacherType = Attacher::AttachEngine3D
  AttachmentSupport = -> [Clone031,Clone001]
  Fuse = false
  MapMode = 49
  Objects = -> [Link003]
  Placement = pos=(325,-207.5,1280) rot=(0,0.707107,0.707107;3.14159rad)
  Scale = (1,1,1)
FEATURE [Part::FeaturePython] Clone052  label="TPDB-2020-015"  # Draft clone (typed FeaturePython)
  AttacherType = Attacher::AttachEngine3D
  AttachmentSupport = -> [Clone031,Clone001]
  Fuse = false
  MapMode = 49
  Objects = -> [Link003]
  Placement = pos=(325,207.5,1280) rot=(0,0.707107,0.707107;3.14159rad)
  Scale = (1,1,1)
FEATURE [Part::FeaturePython] Clone053  label="TPDB-2020-016"  # Draft clone (typed FeaturePython)
  AttacherType = Attacher::AttachEngine3D
  AttachmentSupport = -> [Clone031,Clone001]
  Fuse = false
  MapMode = 49
  Objects = -> [Link003]
  Placement = pos=(-325,207.5,1280) rot=(1,0,0;1.5708rad)
  Scale = (1,1,1)
FEATURE [Part::FeaturePython] Clone054  label="TPDB-2020-017"  # Draft clone (typed FeaturePython)
  AttacherType = Attacher::AttachEngine3D
  AttachmentOffset = pos=(0,10,0) rot=(0,0,1;0rad)
  AttachmentSupport = -> [Clone030,Clone001]
  Fuse = false
  MapMode = 49
  Objects = -> [Link003]
  Placement = pos=(335,-197.5,1280) rot=(0.57735,0.57735,0.57735;2.0944rad)
  Scale = (1,1,1)
FEATURE [Part::FeaturePython] Clone055  label="TPDB-2020-018"  # Draft clone (typed FeaturePython)
  AttacherType = Attacher::AttachEngine3D
  AttachmentOffset = pos=(0,10,0) rot=(0,0,1;0rad)
  AttachmentSupport = -> [Clone030,Clone001]
  Fuse = false
  MapMode = 49
  Objects = -> [Link003]
  Placement = pos=(335,197.5,1280) rot=(0.57735,-0.57735,-0.57735;2.0944rad)
  Scale = (1,1,1)
FEATURE [Part::FeaturePython] Clone056  label="TPDB-2020-019"  # Draft clone (typed FeaturePython)
  AttacherType = Attacher::AttachEngine3D
  AttachmentOffset = pos=(0,10,0) rot=(0,0,1;0rad)
  AttachmentSupport = -> [Clone030,Clone001]
  Fuse = false
  MapMode = 49
  Objects = -> [Link003]
  Placement = pos=(-335,197.5,1280) rot=(0.57735,-0.57735,-0.57735;2.0944rad)
  Scale = (1,1,1)
FEATURE [Part::FeaturePython] Clone057  label="TPDB-2020-020"  # Draft clone (typed FeaturePython)
  AttacherType = Attacher::AttachEngine3D
  AttachmentOffset = pos=(0,10,0) rot=(0,0,1;0rad)
  AttachmentSupport = -> [Clone030,Clone001]
  Fuse = false
  MapMode = 49
  Objects = -> [Link003]
  Placement = pos=(-335,-197.5,1280) rot=(0.57735,0.57735,0.57735;2.0944rad)
  Scale = (1,1,1)
FEATURE [App::DocumentObjectGroup] Group006  label="TPDB-2020"
  Group = -> [Clone028,Clone029,Clone032,Clone033,Clone034,Clone035,Clone036,Clone037,Clone038,Clone039,Clone040,Clone041,Clone050,Clone051,Clone052,Clone053,Clone054,Clone055,Clone056,Clone057]
FEATURE [Sketcher::SketchObject] Sketch027
  ArcFitTolerance = 1e-06
  AttachmentOffset = pos=(0,0,1500) rot=(0,0,1;0rad)
  AttachmentSupport = -> [XY_Plane]
  ExternalGeometry = -> [Binder]
  FullyConstrained = true
  MakeInternals = false
  MapMode = 5
  Placement = pos=(0,0,1500) rot=(0,0,1;0rad)
  sketch-geometry (4):
    g0: LineSegment StartX=-325 StartY=207.5 StartZ=0 EndX=325 EndY=207.5 EndZ=0
    g1: LineSegment StartX=-335 StartY=197.5 StartZ=0 EndX=-335 EndY=-197.5 EndZ=0
    g2: LineSegment StartX=335 StartY=197.5 StartZ=0 EndX=335 EndY=-197.5 EndZ=0
    g3: LineSegment StartX=-325 StartY=-207.5 StartZ=0 EndX=325 EndY=-207.5 EndZ=0
  constraints (16):
    c: Horizontal(g0)
    c: Vertical(g1)
    c: Vertical(g2)
    c: Horizontal(g3)
    c: Equal(g0,g3)
    c: Equal(g1,g2)
    c: Vertical(g-3,g1)
    c: Vertical(g0,g3)
    c: Vertical(g-4,g2)
    c: Horizontal(g0,g-3)
    c: Horizontal(g1,g2)
    c: Horizontal(g-5,g3)
    c: Distance(g-3,g1) = 10
    c: Distance(g1,g-5) = 10
    c: DistanceX(g-3,g0) = 10
    c: DistanceX(g0,g-4) = 10
FEATURE [PartDesign::SubShapeBinder] Binder013  label="Binder019"
  BindCopyOnChange = 0
  BindMode = 0
  ClaimChildren = false
  Context = -> Body [Binder013.]
  Fuse = false
  MakeFace = true
  OffsetFill = false
  OffsetIntersection = false
  OffsetJoinType = 0
  OffsetOpenResult = false
  PartialLoad = false
  Relative = true
  Support = -> [Sketch027]
  _Version = 2
FEATURE [PartDesign::Body] Body
  AllowCompound = true
  Group = -> [Sketch,Sketch001,Pad,Binder,Sketch018,Binder008,Binder009,Binder010,Sketch025,Sketch026,Binder011,Binder012,Sketch027,Binder013]
  Origin = -> Origin
  Tip = -> Pad
FEATURE [Part::FeaturePython] Clone058  label="Binder020"  # Draft clone (typed FeaturePython)
  AttacherType = Attacher::AttachEngine3D
  Fuse = false
  Objects = -> [Binder013]
  Scale = (1,1,1)
FEATURE [Part::FeaturePython] Clone059  label="2020 Profile004"  # Draft clone (typed FeaturePython)
  AttacherType = Attacher::AttachEngine3D
  Fuse = false
  Objects = -> [Binder001]
  Scale = (1,1,1)
FEATURE [Part::FeaturePython] Frame011  # Arch/BIM 107 (typed FeaturePython)
  Align = true
  Base = -> Clone058
  BasePoint = 0
  Edges = 0
  Fuse = false
  HorizontalArea = 0
  IfcData = attributes={"GlobalId": {"name": "GlobalId", "type": "IfcGloballyUniqueId", "is_enum": false, "enum_values": []}, "Description": {"... (+458 chars omitted),+1 more (map truncated)
  IfcType = 107
  MoveBase = false
  MoveWithHost = false
  Offset = (0,0,0)
  PerimeterLength = 0
  PredefinedType = 0
  Profile = -> Clone059
  Rotation = 0
  VerticalArea = 0
FEATURE [Part::FeaturePython] Array  # Draft array (typed FeaturePython)
  AlwaysSyncPlacement = false
  Angle = 360
  ArrayType = 0
  Axis = (0,0,1)
  Base = -> Frame011
  Center = (0,0,0)
  Count = 3
  ExpandArray = false
  Fuse = true
  IntervalAxis = (0,0,0)
  IntervalX = (0,0,0)
  IntervalY = (0,0,0)
  IntervalZ = (0,0,300)
  NumberCircles = 3
  NumberPolar = 5
  NumberX = 1
  NumberY = 1
  NumberZ = 3
  PlacementList = 3 placements: arithmetic series from (0,0,0) step (0,0,300) to (0,0,600)
  RadialDistance = 50
  ScaleList = (3) [(1,1,1),(1,1,1),(1,1,1)]
  Symmetry = 1
  TangentialDistance = 25
FEATURE [PartDesign::SubShapeBinder] Binder014  label="Binder021"
  BindCopyOnChange = 0
  BindMode = 0
  ClaimChildren = false
  Context = -> Body013 [Binder014.]
  Fuse = false
  MakeFace = true
  OffsetFill = false
  OffsetIntersection = false
  OffsetJoinType = 0
  OffsetOpenResult = false
  PartialLoad = false
  Relative = true
  Support = -> [Body[Binder.]]
  _Version = 2
FEATURE [Sketcher::SketchObject] Sketch028
  ArcFitTolerance = 1e-06
  AttachmentSupport = -> [XY_Plane013]
  ExternalGeometry = -> [Binder014]
  FullyConstrained = true
  MakeInternals = false
  MapMode = 5
  sketch-geometry (5):
    g0: LineSegment StartX=315 StartY=-197.5 StartZ=0 EndX=315 EndY=197.5 EndZ=0
    g1: LineSegment StartX=315 StartY=197.5 StartZ=0 EndX=-315 EndY=197.5 EndZ=0
    g2: LineSegment StartX=-315 StartY=197.5 StartZ=0 EndX=-315 EndY=-197.5 EndZ=0
    g3: LineSegment StartX=-315 StartY=-197.5 StartZ=0 EndX=315 EndY=-197.5 EndZ=0
    g4: GeomPoint [constr] X=0 Y=0 Z=0
  constraints (12):
    c: Coincident(g0,g1)
    c: Coincident(g1,g2)
    c: Coincident(g2,g3)
    c: Coincident(g3,g0)
    c: Vertical(g0)
    c: Vertical(g2)
    c: Horizontal(g1)
    c: Horizontal(g3)
    c: Symmetric(g2,g0,g4)
    c: Coincident(g4,g-1)
    c: DistanceX(g-3,g1) = 20
    c: DistanceY(g1,g-3) = 10
FEATURE [PartDesign::Pad] Pad017
  Direction = (0,0,1)
  Length = 310
  Length2 = 10
  Profile = -> Sketch028
  ReferenceAxis = -> Sketch028 [N_Axis]
  Suppressed = false
  Type = 0
FEATURE [PartDesign::SubShapeBinder] Binder015  label="Binder022"
  BindCopyOnChange = 0
  BindMode = 0
  ClaimChildren = false
  Context = -> Body013 [Binder015.]
  Fuse = false
  MakeFace = true
  OffsetFill = false
  OffsetIntersection = false
  OffsetJoinType = 0
  OffsetOpenResult = false
  PartialLoad = false
  Relative = true
  Support = -> [Pad017[Edge2,Edge5,Edge8,Edge1]]
  _Version = 2
FEATURE [PartDesign::Body] Body013
  AllowCompound = true
  Group = -> [Sketch028,Binder014,Pad017,Binder015]
  Origin = -> Origin013
  Tip = -> Pad017
FEATURE [App::DocumentObjectGroup] Group  label="Frame Paths"
  Group = -> [Body,Body010,Body013]
FEATURE [Part::FeaturePython] Clone060  label="Binder023"  # Draft clone (typed FeaturePython)
  AttacherType = Attacher::AttachEngine3D
  Fuse = false
  Objects = -> [Binder015]
  Scale = (1,1,1)
FEATURE [Part::FeaturePython] Clone014  label="TPDC-6034-003"  # Draft clone (typed FeaturePython)
  AttacherType = Attacher::AttachEngine3D
  AttachmentOffset = pos=(0,0,0) rot=(0,0,1;3.14159rad)
  AttachmentSupport = -> [Clone060,Clone016]
  Fuse = false
  MapMode = 49
  Objects = -> [Link]
  Placement = pos=(315,197.5,310) rot=(0.57735,-0.57735,-0.57735;4.18879rad)
  Scale = (1,1,1)
FEATURE [Part::FeaturePython] Clone015  label="TPDC-6034-004"  # Draft clone (typed FeaturePython)
  AttacherType = Attacher::AttachEngine3D
  AttachmentSupport = -> [Clone060,Clone016]
  Fuse = false
  MapMode = 49
  Objects = -> [Link]
  Placement = pos=(-315,197.5,310) rot=(-0.57735,-0.57735,0.57735;4.18879rad)
  Scale = (1,1,1)
FEATURE [Part::FeaturePython] Clone061  label="2040 Profile004"  # Draft clone (typed FeaturePython)
  AttacherType = Attacher::AttachEngine3D
  Fuse = false
  Objects = -> [Binder003]
  Scale = (1,1,1)
FEATURE [Part::FeaturePython] Frame012  # Arch/BIM 107 (typed FeaturePython)
  Align = true
  Base = -> Clone060
  BasePoint = 0
  Edges = 0
  Fuse = false
  HorizontalArea = 0
  IfcData = attributes={"GlobalId": {"name": "GlobalId", "type": "IfcGloballyUniqueId", "is_enum": false, "enum_values": []}, "Description": {"... (+458 chars omitted),+1 more (map truncated)
  IfcType = 107
  MoveBase = false
  MoveWithHost = false
  Offset = (0,0,0)
  PerimeterLength = 0
  PredefinedType = 0
  Profile = -> Clone061
  Rotation = 90
  VerticalArea = 0
FEATURE [App::DocumentObjectGroup] Group002  label="Frames"
  Group = -> [Frame,Frame003,Frame004,Frame005,Frame006,Frame009,Frame010,Frame011,Array,Frame012]
FEATURE [Part::FeaturePython] Clone062  label="TPDC-6034-009"  # Draft clone (typed FeaturePython)
  AttacherType = Attacher::AttachEngine3D
  AttachmentOffset = pos=(0,0,-10) rot=(0,0,1;0rad)
  AttachmentSupport = -> [Clone006,Clone018]
  Fuse = false
  MapMode = 49
  Objects = -> [Link]
  Placement = pos=(-325,187.5,310) rot=(-0.707107,0,0.707107;3.14159rad)
  Scale = (1,1,1)
FEATURE [Part::FeaturePython] Clone063  label="TPDC-6034-010"  # Draft clone (typed FeaturePython)
  AttacherType = Attacher::AttachEngine3D
  AttachmentOffset = pos=(0,0,10) rot=(0,0,1;3.14159rad)
  AttachmentSupport = -> [Clone006,Clone018]
  Fuse = false
  MapMode = 49
  Objects = -> [Link]
  Placement = pos=(-325,-187.5,310) rot=(0,-1,0;4.71239rad)
  Scale = (1,1,1)
FEATURE [Part::FeaturePython] Clone064  label="TPDC-6034-011"  # Draft clone (typed FeaturePython)
  AttacherType = Attacher::AttachEngine3D
  AttachmentOffset = pos=(0,0,-10) rot=(0,0,1;3.14159rad)
  AttachmentSupport = -> [Clone006,Clone018]
  Fuse = false
  MapMode = 49
  Objects = -> [Link]
  Placement = pos=(325,-187.5,310) rot=(0,-1,0;4.71239rad)
  Scale = (1,1,1)
FEATURE [Part::FeaturePython] Clone065  label="TPDC-6034-012"  # Draft clone (typed FeaturePython)
  AttacherType = Attacher::AttachEngine3D
  AttachmentOffset = pos=(0,0,10) rot=(0,0,1;0rad)
  AttachmentSupport = -> [Clone006,Clone018]
  Fuse = false
  MapMode = 49
  Objects = -> [Link]
  Placement = pos=(325,187.5,310) rot=(-0.707107,0,0.707107;3.14159rad)
  Scale = (1,1,1)
FEATURE [App::DocumentObjectGroup] Group005  label="TPDC-6034"
  Group = -> [Clone012,Clone013,Clone014,Clone015,Clone022,Clone023,Clone024,Clone025,Clone062,Clone063,Clone064,Clone065]
FEATURE [TechDraw::DrawSVGTemplate] Template
  Height = 297
  Orientation = 0
  Template = /Applications/FreeCAD.app/Contents/Resources/share/Mod/TechDraw/Templates/A4_Portrait_blank.svg
  Width = 210
FEATURE [TechDraw::DrawProjGroupItem] View  label="Front"
  CoarseView = false
  Direction = (0,-1,0)
  Focus = 100
  HardHidden = false
  IsoCount = 0
  IsoHidden = false
  IsoVisible = false
  LockPosition = true
  Perspective = false
  Rotation = 0
  RotationVector = (1,0,0)
  Scale = 0.1
  ScaleType = 2
  ScrubCount = 1
  SeamHidden = false
  SeamVisible = false
  SmoothHidden = false
  SmoothVisible = true
  Source = -> [Group002,Group003,Group005,Group006,Group008]
  Type = 0
  X = 0
  XDirection = (1,0,0)
  Y = 0
FEATURE [TechDraw::DrawProjGroupItem] ProjItem  label="Right"
  CoarseView = false
  Direction = (1,-1e-16,0)
  Focus = 100
  HardHidden = false
  IsoCount = 0
  IsoHidden = false
  IsoVisible = false
  LockPosition = false
  Perspective = false
  Rotation = 0
  RotationVector = (1,0,0)
  ScaleType = 0
  ScrubCount = 1
  SeamHidden = false
  SeamVisible = false
  SmoothHidden = false
  SmoothVisible = true
  Source = -> [Group002,Group003,Group005,Group006,Group008]
  Type = 2
  X = 71.25
  XDirection = (1e-16,1,0)
  Y = 0
FEATURE [TechDraw::DrawProjGroup] ProjGroup
  Anchor = -> View
  AutoDistribute = true
  LockPosition = false
  ProjectionType = 1
  Rotation = 0
  Scale = 0.1
  ScaleType = 2
  Source = -> [Group002,Group003,Group005,Group006,Group008]
  Views = -> [View,ProjItem]
  X = 81.7862
  Y = 156.194
  spacingX = 15
  spacingY = 15
FEATURE [TechDraw::DrawViewBalloon] Balloon
  BubbleShape = 1
  EndType = 0
  EndTypeScale = 1
  KinkLength = 5
  LockPosition = false
  OriginX = -306.5
  OriginY = -1045
  Rotation = 0
  ScaleType = 0
  ShapeScale = 1
  SourceView = -> View
  Text = 2040x310mm
  TextWrapLen = -1
  X = -38.3904
  Y = -985.916
FEATURE [TechDraw::DrawViewBalloon] Balloon001
  BubbleShape = 1
  EndType = 0
  EndTypeScale = 1
  KinkLength = 5
  LockPosition = false
  OriginX = 204.718
  OriginY = -864.623
  Rotation = 0
  ScaleType = 0
  ShapeScale = 1
  SourceView = -> View
  Text = 2040x650mm
  TextWrapLen = -1
  X = -607.532
  Y = -744.476
FEATURE [TechDraw::DrawViewBalloon] Balloon002
  BubbleShape = 1
  EndType = 0
  EndTypeScale = 1
  KinkLength = 5
  LockPosition = false
  OriginX = -179
  OriginY = -1045
  Rotation = 0
  ScaleType = 0
  ShapeScale = 1
  SourceView = -> ProjItem
  Text = 2020x310mm
  TextWrapLen = -1
  X = 49.6695
  Y = -1010.65
FEATURE [TechDraw::DrawViewBalloon] Balloon003
  BubbleShape = 1
  EndType = 0
  EndTypeScale = 1
  KinkLength = 5
  LockPosition = false
  OriginX = 120.574
  OriginY = -866.618
  Rotation = 0
  ScaleType = 0
  ShapeScale = 1
  SourceView = -> ProjItem
  Text = 4420x395mm
  TextWrapLen = -1
  X = -20.2749
  Y = -660.247
FEATURE [TechDraw::DrawViewBalloon] Balloon004
  BubbleShape = 1
  EndType = 0
  EndTypeScale = 1
  KinkLength = 5
  LockPosition = false
  OriginX = 0
  OriginY = 83.6
  Rotation = 0
  ScaleType = 0
  ShapeScale = 1
  SourceView = -> View
  Text = 2020x650mm
  TextWrapLen = -1
  X = 120.362
  Y = 216.704
FEATURE [TechDraw::DrawViewBalloon] Balloon006
  BubbleShape = 1
  EndType = 0
  EndTypeScale = 1
  KinkLength = 5
  LockPosition = false
  OriginX = 0
  OriginY = 88.5
  Rotation = 0
  ScaleType = 0
  ShapeScale = 1
  SourceView = -> ProjItem
  Text = 2040x395mm
  TextWrapLen = -1
  X = 384.559
  Y = 155.05
FEATURE [TechDraw::DrawPage] Page
  KeepUpdated = true
  NextBalloonIndex = 9
  ProjectionType = 0
  Template = -> Template
  Views = -> [ProjGroup,Balloon,Balloon001,Balloon002,Balloon003,Balloon004,Balloon006]
FEATURE [TechDraw::DrawSVGTemplate] Template001
  Height = 210
  Orientation = 1
  Template = /Applications/FreeCAD.app/Contents/Resources/share/Mod/TechDraw/Templates/A4_Landscape_blank.svg
  Width = 297
FEATURE [TechDraw::DrawProjGroupItem] View001
  CoarseView = false
  Direction = (0,0,1)
  Focus = 100
  HardHidden = false
  IsoCount = 0
  IsoHidden = false
  IsoVisible = false
  LockPosition = false
  Perspective = false
  Rotation = 0
  RotationVector = (1,0,0)
  Scale = 0.2
  ScaleType = 2
  ScrubCount = 1
  SeamHidden = false
  SeamVisible = false
  SmoothHidden = false
  SmoothVisible = true
  Source = -> [Group005,Group002]
  Type = 0
  X = 148.5
  XDirection = (1,0,0)
  Y = 105
FEATURE [TechDraw::DrawViewBalloon] Balloon007
  BubbleShape = 1
  EndType = 0
  EndTypeScale = 1
  KinkLength = 5
  LockPosition = false
  OriginX = 0
  OriginY = 177.5
  Rotation = 0
  ScaleType = 0
  ShapeScale = 1
  SourceView = -> View001
  Text = 2040x610mm
  TextWrapLen = -1
  X = 139.352
  Y = 273.692
FEATURE [TechDraw::DrawPage] Page001
  KeepUpdated = true
  NextBalloonIndex = 3
  ProjectionType = 0
  Template = -> Template001
  Views = -> [View001,Balloon007]
